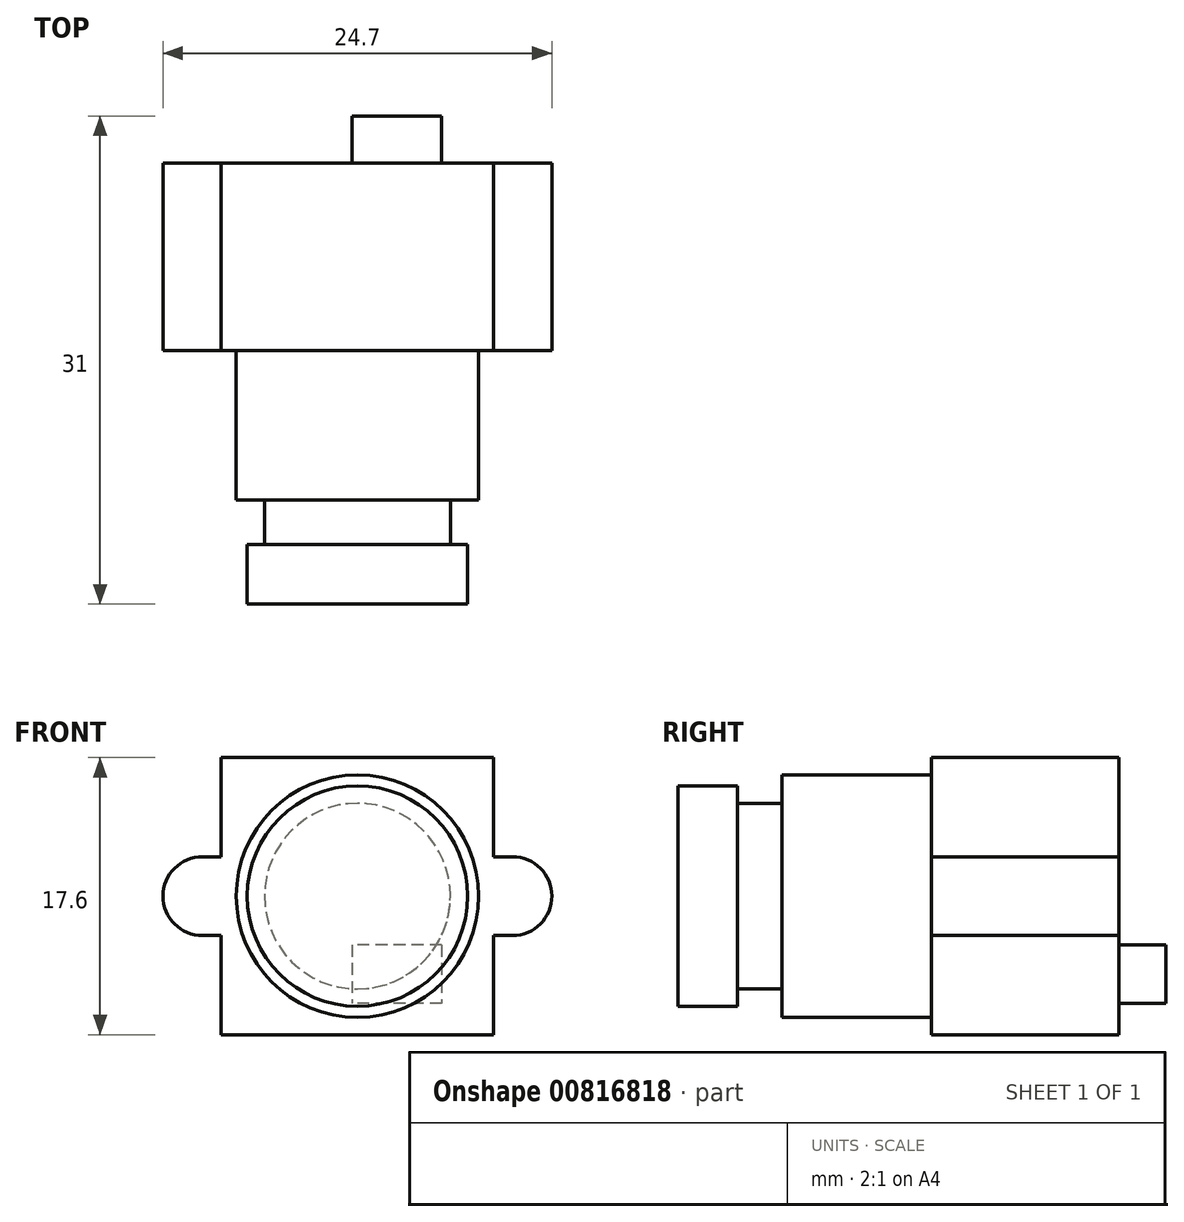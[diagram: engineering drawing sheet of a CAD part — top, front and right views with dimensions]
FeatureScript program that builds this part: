
annotation { "Feature Type Name" : "Feature", "Feature Type Description" : "" }
export const myFeature = defineFeature(function(context is Context, id is Id, definition is map)
    precondition{}
    {
        {
            var Q0;
            Q0=qCreatedBy(makeId("Front.planeOp"),FACE);
            var sketch = newSketch(context, id + "F0", { "sketchPlane" : qUnion([Q0])});
            skLineSegment(sketch, "E0.bottom", {"start": v(-8.65, 17.6) * mm, "end": v(8.65, 17.6) * mm});
            skLineSegment(sketch, "E0.top", {"start": v(-8.65, 0) * mm, "end": v(8.65, 0) * mm});
            skLineSegment(sketch, "E0.left", {"start": v(-8.65, 17.6) * mm, "end": v(-8.65, 11.3) * mm});
            skLineSegment(sketch, "E0.right", {"start": v(8.65, 17.6) * mm, "end": v(8.65, 11.3) * mm});
            skArc(sketch, "E1", {"start": v(-9.85, 11.3) * mm, "mid": v(-12.35, 8.8) * mm, "end": v(-9.85, 6.3) * mm});
            skArc(sketch, "E2", {"start": v(9.85, 6.3) * mm, "mid": v(12.35, 8.8) * mm, "end": v(9.85, 11.3) * mm});
            skLineSegment(sketch, "E3", {"start": v(-16.4, 8.8) * mm, "end": v(17.39, 8.8) * mm, "construction": true});
            skLineSegment(sketch, "E4", {"start": v(-9.85, 11.3) * mm, "end": v(-8.65, 11.3) * mm});
            skLineSegment(sketch, "E5", {"start": v(-9.85, 6.3) * mm, "end": v(-8.65, 6.3) * mm});
            skLineSegment(sketch, "E6.trimOffspring", {"start": v(8.65, 11.3) * mm, "end": v(9.85, 11.3) * mm});
            skLineSegment(sketch, "E7.trimOffspring", {"start": v(-8.65, 6.3) * mm, "end": v(-8.65, 0) * mm});
            skLineSegment(sketch, "E8.trimOffspring", {"start": v(8.65, 6.3) * mm, "end": v(9.85, 6.3) * mm});
            skLineSegment(sketch, "E9.trimOffspring", {"start": v(8.65, 6.3) * mm, "end": v(8.65, 0) * mm});
            skSolve(sketch);
        }
        {
            var Q0;
            Q0=makeQuery(id+"F0.imprint","IMPRINT",FACE,{"disambiguationData":[TD([[makeQuery(id+"F0.imprint","IMPRINT",EDGE,{"derivedFrom":sQuery(id+"F0.wireOp",EDGE,"E0.bottom")}),-1.0]])]});
            extrude(context, id + "F1", {"entities" : qUnion([Q0]), "depth" : 11.9 * mm, "offsetDistance" : 25 * mm});
        }
        {
            var Q0;
            Q0=makeQuery(id+"F1.opExtrude","CAP_FACE",FACE,{"disambiguationData":[OSD([sQuery(id+"F0.wireOp",EDGE,"E0.bottom"),sQuery(id+"F0.wireOp",EDGE,"E0.top"),sQuery(id+"F0.wireOp",EDGE,"E0.left"),sQuery(id+"F0.wireOp",EDGE,"E0.right"),sQuery(id+"F0.wireOp",EDGE,"E1"),sQuery(id+"F0.wireOp",EDGE,"E2"),sQuery(id+"F0.wireOp",EDGE,"E4"),sQuery(id+"F0.wireOp",EDGE,"E5"),sQuery(id+"F0.wireOp",EDGE,"E6.trimOffspring"),sQuery(id+"F0.wireOp",EDGE,"E7.trimOffspring"),sQuery(id+"F0.wireOp",EDGE,"E8.trimOffspring"),sQuery(id+"F0.wireOp",EDGE,"E9.trimOffspring")])],"isStart":false});
            var sketch = newSketch(context, id + "F2", { "sketchPlane" : qUnion([Q0])});
            skCircle(sketch, "E10", {"center": v(0, 8.8) * mm, "radius": 7.7 * mm});
            skSolve(sketch);
        }
        {
            var Q0;
            Q0=makeQuery(id+"F2.imprint","IMPRINT",FACE,{"disambiguationData":[TD([[makeQuery(id+"F2.imprint","IMPRINT",EDGE,{"derivedFrom":sQuery(id+"F2.wireOp",EDGE,"E10")}),1.0]])]});
            extrude(context, id + "F3", {"entities" : qUnion([Q0]), "operationType" : NewBodyOperationType.ADD, "depth" : 9.5 * mm, "offsetDistance" : 25 * mm});
        }
        {
            var Q0;
            Q0=qCreatedBy(makeId("Front.planeOp"),FACE);
            cPlane(context, id + "F4", {"entities" : qUnion([Q0]), "cplaneType" : CPlaneType.OFFSET, "offset" : 28 * mm, "width" : 150 * mm, "height" : 150 * mm});
        }
        {
            var Q0;
            Q0=qCreatedBy(id+"F4.planeOp",FACE);
            var sketch = newSketch(context, id + "F5", { "sketchPlane" : qUnion([Q0])});
            skCircle(sketch, "E11", {"center": v(0, 8.8) * mm, "radius": 7 * mm});
            skSolve(sketch);
        }
        {
            var Q0;
            Q0=makeQuery(id+"F5.imprint","IMPRINT",FACE,{"disambiguationData":[TD([[makeQuery(id+"F5.imprint","IMPRINT",EDGE,{"derivedFrom":sQuery(id+"F5.wireOp",EDGE,"E11")}),1.0]])]});
            extrude(context, id + "F6", {"entities" : qUnion([Q0]), "oppositeDirection" : true, "depth" : 3.8 * mm, "offsetDistance" : 25 * mm});
        }
        {
            var Q0;
            Q0=makeQuery(id+"F6.opExtrude","CAP_FACE",FACE,{"disambiguationData":[OSD([sQuery(id+"F5.wireOp",EDGE,"E11")])],"isStart":false});
            var sketch = newSketch(context, id + "F7", { "sketchPlane" : qUnion([Q0])});
            skCircle(sketch, "E12", {"center": v(0, 8.8) * mm, "radius": 5.9 * mm});
            skSolve(sketch);
        }
        {
            var Q0;
            Q0=makeQuery(id+"F7.imprint","IMPRINT",FACE,{"disambiguationData":[TD([[makeQuery(id+"F7.imprint","IMPRINT",EDGE,{"derivedFrom":sQuery(id+"F7.wireOp",EDGE,"E12")}),1.0]])]});
            var Q1;
            Q1=makeQuery(id+"F1.opExtrude","SWEPT_BODY",BODY,{"disambiguationData":[OSD([sQuery(id+"F0.wireOp",EDGE,"E0.bottom"),sQuery(id+"F0.wireOp",EDGE,"E0.top"),sQuery(id+"F0.wireOp",EDGE,"E0.left"),sQuery(id+"F0.wireOp",EDGE,"E0.right"),sQuery(id+"F0.wireOp",EDGE,"E1"),sQuery(id+"F0.wireOp",EDGE,"E2"),sQuery(id+"F0.wireOp",EDGE,"E4"),sQuery(id+"F0.wireOp",EDGE,"E5"),sQuery(id+"F0.wireOp",EDGE,"E6.trimOffspring"),sQuery(id+"F0.wireOp",EDGE,"E7.trimOffspring"),sQuery(id+"F0.wireOp",EDGE,"E8.trimOffspring"),sQuery(id+"F0.wireOp",EDGE,"E9.trimOffspring")])]});
            extrude(context, id + "F8", {"entities" : qUnion([Q0]), "operationType" : NewBodyOperationType.ADD, "endBound" : BoundingType.UP_TO_BODY, "depth" : 25 * mm, "endBoundEntityBody" : qUnion([Q1]), "offsetDistance" : 25 * mm});
        }
        {
            var Q0;
            Q0=makeQuery(id+"F0.imprint","IMPRINT",FACE,{"disambiguationData":[TD([[makeQuery(id+"F0.imprint","IMPRINT",EDGE,{"derivedFrom":sQuery(id+"F0.wireOp",EDGE,"E0.bottom")}),-1.0]])]});
            var sketch = newSketch(context, id + "F9", { "sketchPlane" : qUnion([Q0])});
            skLineSegment(sketch, "E13.bottom", {"start": v(5.35, 5.7) * mm, "end": v(-0.35, 5.7) * mm});
            skLineSegment(sketch, "E13.top", {"start": v(5.35, 2) * mm, "end": v(-0.35, 2) * mm});
            skLineSegment(sketch, "E13.left", {"start": v(5.35, 5.7) * mm, "end": v(5.35, 2) * mm});
            skLineSegment(sketch, "E13.right", {"start": v(-0.35, 5.7) * mm, "end": v(-0.35, 2) * mm});
            skSolve(sketch);
        }
        {
            var Q0;
            Q0=makeQuery(id+"F9.imprint","IMPRINT",FACE,{"disambiguationData":[TD([[makeQuery(id+"F9.imprint","IMPRINT",EDGE,{"derivedFrom":sQuery(id+"F9.wireOp",EDGE,"E13.bottom")}),1.0]])]});
            extrude(context, id + "F10", {"entities" : qUnion([Q0]), "oppositeDirection" : true, "depth" : 3 * mm, "offsetDistance" : 25 * mm});
        }
    });
